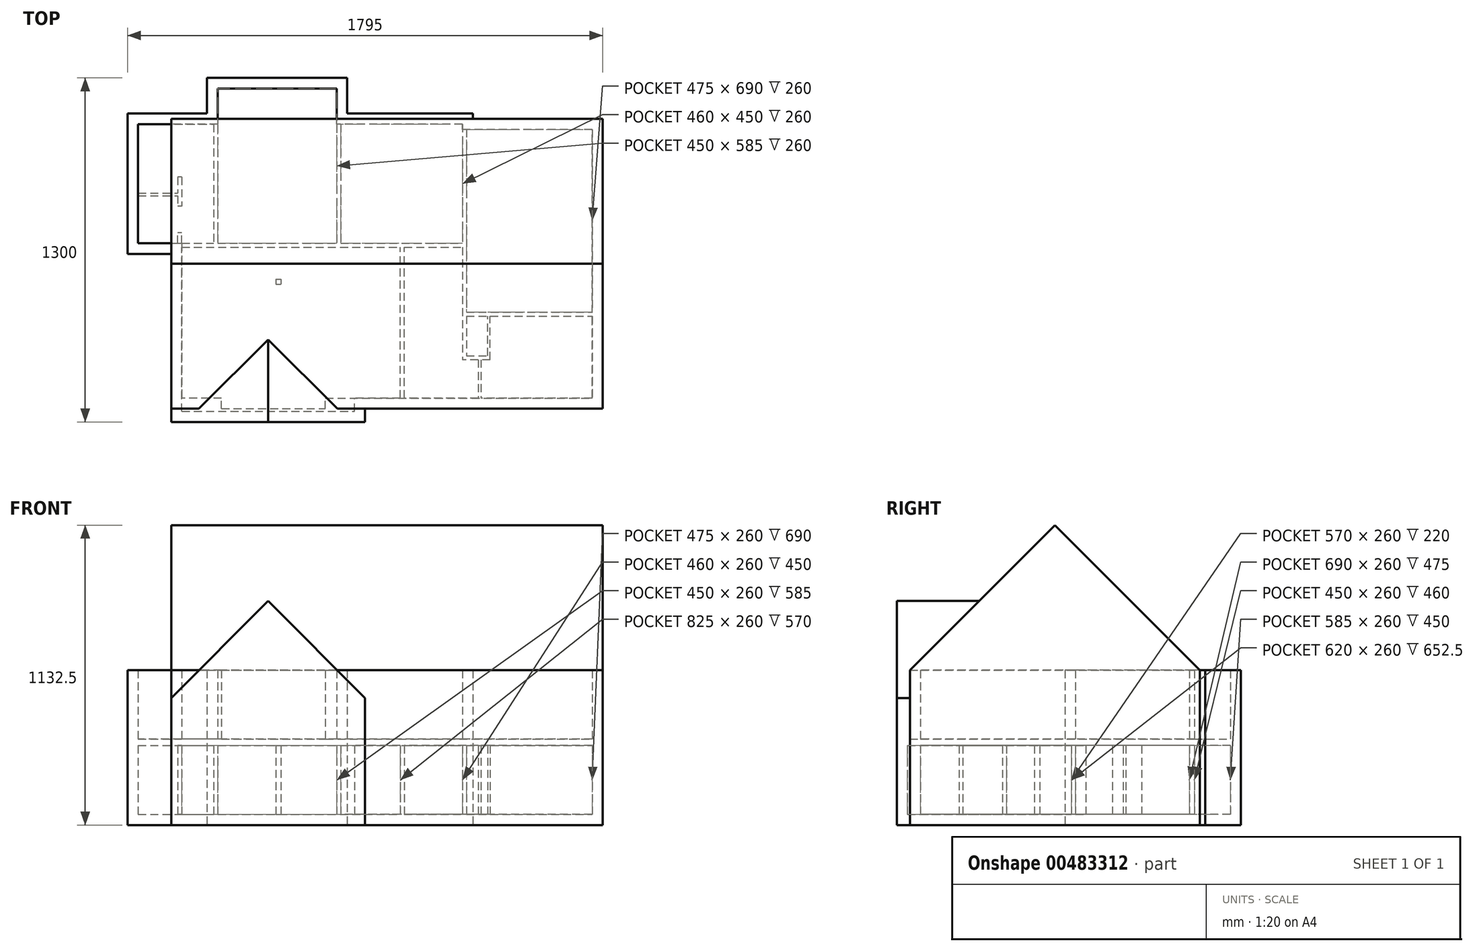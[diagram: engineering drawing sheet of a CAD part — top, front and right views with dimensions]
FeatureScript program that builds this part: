
annotation { "Feature Type Name" : "Feature", "Feature Type Description" : "" }
export const myFeature = defineFeature(function(context is Context, id is Id, definition is map)
    precondition{}
    {
        {
            var Q0;
            Q0=qCreatedBy(makeId("Top.planeOp"),FACE);
            var sketch = newSketch(context, id + "F0", { "sketchPlane" : qUnion([Q0])});
            skLineSegment(sketch, "E0.bottom", {"start": v(-897.5, 650) * mm, "end": v(897.5, 650) * mm});
            skLineSegment(sketch, "E0.top", {"start": v(-897.5, -650) * mm, "end": v(897.5, -650) * mm});
            skLineSegment(sketch, "E0.left", {"start": v(-897.5, 650) * mm, "end": v(-897.5, -650) * mm});
            skLineSegment(sketch, "E0.right", {"start": v(897.5, 650) * mm, "end": v(897.5, -650) * mm});
            skPoint(sketch, "E0.middle", {"position": v(0, 0) * mm});
            skSolve(sketch);
        }
        {
            var Q0;
            Q0 = qSketchRegion(id + "F0", true);
            extrude(context, id + "F1", {"entities" : qUnion([Q0]), "depth" : 300 * mm});
        }
        {
            var Q0;
            Q0=makeQuery(id+"F1.opExtrude","CAP_FACE",FACE,{"disambiguationData":[OSD([sQuery(id+"F0.wireOp",EDGE,"E0.bottom"),sQuery(id+"F0.wireOp",EDGE,"E0.top"),sQuery(id+"F0.wireOp",EDGE,"E0.left"),sQuery(id+"F0.wireOp",EDGE,"E0.right")])],"isStart":true});
            var sketch = newSketch(context, id + "F2", { "sketchPlane" : qUnion([Q0])});
            skLineSegment(sketch, "E1.bottom", {"start": v(-897.5, 650) * mm, "end": v(-732.5, 650) * mm});
            skLineSegment(sketch, "E1.top", {"start": v(-897.5, 15) * mm, "end": v(-732.5, 15) * mm});
            skLineSegment(sketch, "E1.left", {"start": v(-897.5, 650) * mm, "end": v(-897.5, 15) * mm});
            skLineSegment(sketch, "E1.right", {"start": v(-732.5, 650) * mm, "end": v(-732.5, 15) * mm});
            skPoint(sketch, "E2.oppositeSnap0", {"position": v(-732.5, 332.5) * mm});
            skLineSegment(sketch, "E2.bottom", {"start": v(-897.5, -650) * mm, "end": v(-597.5, -650) * mm});
            skLineSegment(sketch, "E2.top", {"start": v(-897.5, -515) * mm, "end": v(-597.5, -515) * mm});
            skLineSegment(sketch, "E2.left", {"start": v(-897.5, -650) * mm, "end": v(-897.5, -515) * mm});
            skLineSegment(sketch, "E2.right", {"start": v(-597.5, -650) * mm, "end": v(-597.5, -515) * mm});
            skLineSegment(sketch, "E3.bottom", {"start": v(897.5, 650) * mm, "end": v(0, 650) * mm});
            skLineSegment(sketch, "E3.top", {"start": v(897.5, 600) * mm, "end": v(0, 600) * mm});
            skLineSegment(sketch, "E3.left", {"start": v(897.5, 650) * mm, "end": v(897.5, 600) * mm});
            skLineSegment(sketch, "E3.right", {"start": v(0, 650) * mm, "end": v(0, 600) * mm});
            skLineSegment(sketch, "E4.bottom", {"start": v(897.5, -650) * mm, "end": v(-67.5, -650) * mm});
            skLineSegment(sketch, "E4.top", {"start": v(897.5, -515) * mm, "end": v(-67.5, -515) * mm});
            skLineSegment(sketch, "E4.left", {"start": v(897.5, -650) * mm, "end": v(897.5, -515) * mm});
            skLineSegment(sketch, "E4.right", {"start": v(-67.5, -650) * mm, "end": v(-67.5, -515) * mm});
            skLineSegment(sketch, "E5.bottom", {"start": v(897.5, -515) * mm, "end": v(407.5, -515) * mm});
            skLineSegment(sketch, "E5.top", {"start": v(897.5, -495) * mm, "end": v(407.5, -495) * mm});
            skLineSegment(sketch, "E5.left", {"start": v(897.5, -515) * mm, "end": v(897.5, -495) * mm});
            skLineSegment(sketch, "E5.right", {"start": v(407.5, -515) * mm, "end": v(407.5, -495) * mm});
            skSolve(sketch);
        }
        {
            var Q0;
            Q0 = qSketchRegion(id + "F2", true);
            extrude(context, id + "F3", {"entities" : qUnion([Q0]), "operationType" : NewBodyOperationType.REMOVE, "oppositeDirection" : true, "depth" : 300 * mm});
        }
        {
            var Q0;
            Q0=makeQuery(id+"F1.opExtrude","CAP_FACE",FACE,{"disambiguationData":[OSD([sQuery(id+"F0.wireOp",EDGE,"E0.bottom"),sQuery(id+"F0.wireOp",EDGE,"E0.top"),sQuery(id+"F0.wireOp",EDGE,"E0.left"),sQuery(id+"F0.wireOp",EDGE,"E0.right")])],"isStart":false});
            shell(context, id + "F4", {"entities" : qUnion([Q0]), "thickness" : 40 * mm});
        }
        {
            var Q0;
            Q0=makeQuery(id+"F4.opShell","OFFSET_FACE",FACE,{"disambiguationData":[OSD([sQuery(id+"F0.wireOp",EDGE,"E0.bottom"),sQuery(id+"F0.wireOp",EDGE,"E0.top"),sQuery(id+"F0.wireOp",EDGE,"E0.left"),sQuery(id+"F0.wireOp",EDGE,"E0.right")])]});
            var sketch = newSketch(context, id + "F5", { "sketchPlane" : qUnion([Q0])});
            skLineSegment(sketch, "E6.bottom", {"start": v(132.5, -560) * mm, "end": v(147.5, -560) * mm});
            skLineSegment(sketch, "E6.left", {"start": v(132.5, -560) * mm, "end": v(132.5, 10) * mm});
            skLineSegment(sketch, "E6.right", {"start": v(147.5, -560) * mm, "end": v(147.5, 10) * mm});
            skLineSegment(sketch, "E7.bottom", {"start": v(382.5, -235) * mm, "end": v(857.5, -235) * mm});
            skLineSegment(sketch, "E7.top", {"start": v(382.5, -250) * mm, "end": v(462.5, -250) * mm});
            skLineSegment(sketch, "E7.right", {"start": v(857.5, -235) * mm, "end": v(857.5, -250) * mm});
            skLineSegment(sketch, "E8.bottom", {"start": v(-692.5, 25) * mm, "end": v(-572.5, 25) * mm});
            skLineSegment(sketch, "E8.top", {"start": v(-692.5, 10) * mm, "end": v(132.5, 10) * mm});
            skLineSegment(sketch, "E8.left", {"start": v(-692.5, 25) * mm, "end": v(-692.5, 10) * mm});
            skLineSegment(sketch, "E9.bottom", {"start": v(-857.5, 205) * mm, "end": v(-707.5, 205) * mm});
            skLineSegment(sketch, "E9.top", {"start": v(-857.5, 215) * mm, "end": v(-707.5, 215) * mm});
            skLineSegment(sketch, "E9.left", {"start": v(-857.5, 215) * mm, "end": v(-857.5, 205) * mm});
            skLineSegment(sketch, "E9.right", {"start": v(-692.5, 215) * mm, "end": v(-692.5, 205) * mm});
            skLineSegment(sketch, "E10.bottom", {"start": v(-107.5, 475) * mm, "end": v(-92.5, 475) * mm});
            skLineSegment(sketch, "E10.left", {"start": v(-107.5, 475) * mm, "end": v(-107.5, 25) * mm});
            skLineSegment(sketch, "E10.right", {"start": v(-92.5, 475) * mm, "end": v(-92.5, 25) * mm});
            skLineSegment(sketch, "E11.bottom", {"start": v(367.5, 455) * mm, "end": v(382.5, 455) * mm});
            skLineSegment(sketch, "E11.left", {"start": v(367.5, 455) * mm, "end": v(367.5, 25) * mm});
            skLineSegment(sketch, "E11.right", {"start": v(382.5, 455) * mm, "end": v(382.5, -235) * mm});
            skLineSegment(sketch, "E12.trimOffspring", {"start": v(382.5, -250) * mm, "end": v(382.5, -400) * mm});
            skLineSegment(sketch, "E13.trimOffspring", {"start": v(-92.5, 25) * mm, "end": v(367.5, 25) * mm});
            skLineSegment(sketch, "E14.bottom", {"start": v(-557.5, 475) * mm, "end": v(-572.5, 475) * mm});
            skLineSegment(sketch, "E14.left", {"start": v(-557.5, 475) * mm, "end": v(-557.5, 25) * mm});
            skLineSegment(sketch, "E14.right", {"start": v(-572.5, 475) * mm, "end": v(-572.5, 25) * mm});
            skLineSegment(sketch, "E15.trimOffspring", {"start": v(-557.5, 25) * mm, "end": v(-107.5, 25) * mm});
            skLineSegment(sketch, "E16.bottom", {"start": v(-692.5, 25) * mm, "end": v(-707.5, 25) * mm});
            skLineSegment(sketch, "E16.top", {"start": v(-692.5, 65) * mm, "end": v(-707.5, 65) * mm});
            skLineSegment(sketch, "E16.left", {"start": v(-692.5, 25) * mm, "end": v(-692.5, 65) * mm});
            skLineSegment(sketch, "E16.right", {"start": v(-707.5, 25) * mm, "end": v(-707.5, 65) * mm});
            skLineSegment(sketch, "E17.bottom", {"start": v(-692.5, 275) * mm, "end": v(-707.5, 275) * mm});
            skLineSegment(sketch, "E17.top", {"start": v(-692.5, 165) * mm, "end": v(-707.5, 165) * mm});
            skLineSegment(sketch, "E17.left", {"start": v(-692.5, 275) * mm, "end": v(-692.5, 165) * mm});
            skLineSegment(sketch, "E17.right", {"start": v(-707.5, 275) * mm, "end": v(-707.5, 215) * mm});
            skLineSegment(sketch, "E18.trimOffspring", {"start": v(-707.5, 205) * mm, "end": v(-707.5, 165) * mm});
            skLineSegment(sketch, "E19.top", {"start": v(147.5, 10) * mm, "end": v(367.5, 10) * mm});
            skLineSegment(sketch, "E20.trimOffspring", {"start": v(367.5, 10) * mm, "end": v(367.5, -415) * mm});
            skLineSegment(sketch, "E21", {"start": v(472.5, -415) * mm, "end": v(472.5, -250) * mm});
            skLineSegment(sketch, "E22", {"start": v(382.5, -400) * mm, "end": v(462.5, -400) * mm});
            skLineSegment(sketch, "E23", {"start": v(462.5, -400) * mm, "end": v(462.5, -250) * mm});
            skLineSegment(sketch, "E24", {"start": v(427.5, -415) * mm, "end": v(427.5, -560) * mm});
            skLineSegment(sketch, "E25", {"start": v(437.5, -415) * mm, "end": v(437.5, -560) * mm});
            skLineSegment(sketch, "E26", {"start": v(472.5, -415) * mm, "end": v(437.5, -415) * mm});
            skLineSegment(sketch, "E27.trimOffspring", {"start": v(427.5, -415) * mm, "end": v(367.5, -415) * mm});
            skLineSegment(sketch, "E28.trimOffspring", {"start": v(472.5, -250) * mm, "end": v(857.5, -250) * mm});
            skLineSegment(sketch, "E29", {"start": v(427.5, -560) * mm, "end": v(437.5, -560) * mm});
            skLineSegment(sketch, "E30.bottom", {"start": v(-337.5, -110) * mm, "end": v(-317.5, -110) * mm});
            skLineSegment(sketch, "E30.top", {"start": v(-337.5, -130) * mm, "end": v(-317.5, -130) * mm});
            skLineSegment(sketch, "E30.left", {"start": v(-337.5, -110) * mm, "end": v(-337.5, -130) * mm});
            skLineSegment(sketch, "E30.right", {"start": v(-317.5, -110) * mm, "end": v(-317.5, -130) * mm});
            skSolve(sketch);
        }
        {
            var Q0;
            Q0 = qSketchRegion(id + "F5", true);
            extrude(context, id + "F6", {"entities" : qUnion([Q0]), "operationType" : NewBodyOperationType.ADD, "depth" : 260 * mm});
        }
        {
            var Q0;
            Q0=makeQuery(id+"F6.boolean.opBoolean","MERGE",FACE,{"derivedFrom":[makeQuery(id+"F1.opExtrude","CAP_FACE",FACE,{"disambiguationData":[OSD([sQuery(id+"F0.wireOp",EDGE,"E0.bottom"),sQuery(id+"F0.wireOp",EDGE,"E0.top"),sQuery(id+"F0.wireOp",EDGE,"E0.left"),sQuery(id+"F0.wireOp",EDGE,"E0.right")])],"isStart":false}),makeQuery(id+"F6.opExtrude","CAP_FACE",FACE,{"disambiguationData":[OSD([sQuery(id+"F5.wireOp",EDGE,"E6.bottom"),sQuery(id+"F5.wireOp",EDGE,"E6.left"),sQuery(id+"F5.wireOp",EDGE,"E6.right"),sQuery(id+"F5.wireOp",EDGE,"E7.bottom"),sQuery(id+"F5.wireOp",EDGE,"E7.top"),sQuery(id+"F5.wireOp",EDGE,"E7.right"),sQuery(id+"F5.wireOp",EDGE,"E8.bottom"),sQuery(id+"F5.wireOp",EDGE,"E8.top"),sQuery(id+"F5.wireOp",EDGE,"E8.left"),sQuery(id+"F5.wireOp",EDGE,"E10.bottom"),sQuery(id+"F5.wireOp",EDGE,"E10.left"),sQuery(id+"F5.wireOp",EDGE,"E10.right"),sQuery(id+"F5.wireOp",EDGE,"E11.bottom"),sQuery(id+"F5.wireOp",EDGE,"E11.left"),sQuery(id+"F5.wireOp",EDGE,"E11.right"),sQuery(id+"F5.wireOp",EDGE,"Mbifjuid-vwa9-f3l3-ZE1X-VHg3meccrZwo"),sQuery(id+"F5.wireOp",EDGE,"E12.trimOffspring"),sQuery(id+"F5.wireOp",EDGE,"E13.trimOffspring"),sQuery(id+"F5.wireOp",EDGE,"E14.bottom"),sQuery(id+"F5.wireOp",EDGE,"E14.left"),sQuery(id+"F5.wireOp",EDGE,"E14.right"),sQuery(id+"F5.wireOp",EDGE,"E15.trimOffspring"),sQuery(id+"F5.wireOp",EDGE,"E19.top"),sQuery(id+"F5.wireOp",EDGE,"E20.trimOffspring")])],"isStart":false}),makeQuery(id+"F6.opExtrude","CAP_FACE",FACE,{"disambiguationData":[OSD([sQuery(id+"F5.wireOp",EDGE,"E9.bottom"),sQuery(id+"F5.wireOp",EDGE,"E9.top"),sQuery(id+"F5.wireOp",EDGE,"E9.left"),sQuery(id+"F5.wireOp",EDGE,"E17.bottom"),sQuery(id+"F5.wireOp",EDGE,"E17.top"),sQuery(id+"F5.wireOp",EDGE,"E17.left"),sQuery(id+"F5.wireOp",EDGE,"E17.right"),sQuery(id+"F5.wireOp",EDGE,"E18.trimOffspring")])],"isStart":false}),makeQuery(id+"F6.opExtrude","CAP_FACE",FACE,{"disambiguationData":[OSD([sQuery(id+"F5.wireOp",EDGE,"E16.bottom"),sQuery(id+"F5.wireOp",EDGE,"E16.top"),sQuery(id+"F5.wireOp",EDGE,"E16.left"),sQuery(id+"F5.wireOp",EDGE,"E16.right")])],"isStart":false})]});
            var sketch = newSketch(context, id + "F7", { "sketchPlane" : qUnion([Q0])});
            skLineSegment(sketch, "E31.0.0", {"start": v(-732.5, -15) * mm, "end": v(-732.5, -650) * mm});
            skLineSegment(sketch, "E31.0.1", {"start": v(-732.5, -650) * mm, "end": v(0, -650) * mm});
            skLineSegment(sketch, "E31.0.2", {"start": v(0, -650) * mm, "end": v(0, -600) * mm});
            skLineSegment(sketch, "E31.0.3", {"start": v(0, -600) * mm, "end": v(897.5, -600) * mm});
            skLineSegment(sketch, "E31.0.4", {"start": v(897.5, -600) * mm, "end": v(897.5, 495) * mm});
            skLineSegment(sketch, "E31.0.5", {"start": v(897.5, 495) * mm, "end": v(407.5, 495) * mm});
            skLineSegment(sketch, "E31.0.6", {"start": v(407.5, 495) * mm, "end": v(407.5, 515) * mm});
            skLineSegment(sketch, "E31.0.7", {"start": v(407.5, 515) * mm, "end": v(-67.5, 515) * mm});
            skLineSegment(sketch, "E31.0.8", {"start": v(-67.5, 515) * mm, "end": v(-67.5, 650) * mm});
            skLineSegment(sketch, "E31.0.9", {"start": v(-67.5, 650) * mm, "end": v(-597.5, 650) * mm});
            skLineSegment(sketch, "E31.0.10", {"start": v(-597.5, 650) * mm, "end": v(-597.5, 515) * mm});
            skLineSegment(sketch, "E31.0.11", {"start": v(-597.5, 515) * mm, "end": v(-897.5, 515) * mm});
            skLineSegment(sketch, "E31.0.12", {"start": v(-897.5, 515) * mm, "end": v(-897.5, -15) * mm});
            skLineSegment(sketch, "E31.0.13", {"start": v(-897.5, -15) * mm, "end": v(-732.5, -15) * mm});
            skSolve(sketch);
        }
        {
            var Q0;
            Q0 = qSketchRegion(id + "F7", true);
            extrude(context, id + "F8", {"entities" : qUnion([Q0]), "operationType" : NewBodyOperationType.ADD, "depth" : 25 * mm});
        }
        {
            var Q0;
            Q0=makeQuery(id+"F8.boolean.opBoolean","MERGE",FACE,{"derivedFrom":[makeQuery(id+"F1.opExtrude","SWEPT_FACE",FACE,{"disambiguationData":[OSD([sQuery(id+"F0.wireOp",EDGE,"E0.top")])]}),makeQuery(id+"F8.opExtrude","SWEPT_FACE",FACE,{"disambiguationData":[OSD([sQuery(id+"F7.wireOp",EDGE,"948ebf68-d73d-4844-9910-1fd970d81693.0.2")])]})]});
            var sketch = newSketch(context, id + "F9", { "sketchPlane" : qUnion([Q0])});
            skLineSegment(sketch, "E32", {"start": v(-732.5, 325) * mm, "end": v(-732.5, 480) * mm});
            skLineSegment(sketch, "E33", {"start": v(-732.5, 480) * mm, "end": v(-366.25, 846.25) * mm});
            skLineSegment(sketch, "E34", {"start": v(-366.25, 846.25) * mm, "end": v(0, 480) * mm});
            skLineSegment(sketch, "E35", {"start": v(0, 480) * mm, "end": v(0, 325) * mm});
            skLineSegment(sketch, "E36.0", {"start": v(-732.5, 325) * mm, "end": v(0, 325) * mm});
            skSolve(sketch);
        }
        {
            var Q0;
            Q0=makeQuery(id+"F9.imprint","IMPRINT",FACE,{"disambiguationData":[TD([[makeQuery(id+"F9.imprint","IMPRINT",EDGE,{"derivedFrom":sQuery(id+"F9.wireOp",EDGE,"E32")}),-1.0]])]});
            extrude(context, id + "F10", {"entities" : qUnion([Q0]), "operationType" : NewBodyOperationType.ADD, "oppositeDirection" : true, "depth" : 50 * mm});
        }
        {
            var Q0;
            Q0=makeQuery(id+"F8.opExtrude","CAP_FACE",FACE,{"disambiguationData":[OSD([sQuery(id+"F7.wireOp",EDGE,"E31.0.0"),sQuery(id+"F7.wireOp",EDGE,"E31.0.1"),sQuery(id+"F7.wireOp",EDGE,"E31.0.2"),sQuery(id+"F7.wireOp",EDGE,"E31.0.3"),sQuery(id+"F7.wireOp",EDGE,"E31.0.4"),sQuery(id+"F7.wireOp",EDGE,"E31.0.5"),sQuery(id+"F7.wireOp",EDGE,"E31.0.6"),sQuery(id+"F7.wireOp",EDGE,"E31.0.7"),sQuery(id+"F7.wireOp",EDGE,"E31.0.8"),sQuery(id+"F7.wireOp",EDGE,"E31.0.9"),sQuery(id+"F7.wireOp",EDGE,"E31.0.10"),sQuery(id+"F7.wireOp",EDGE,"E31.0.11"),sQuery(id+"F7.wireOp",EDGE,"E31.0.12"),sQuery(id+"F7.wireOp",EDGE,"E31.0.13")])],"isStart":false});
            var sketch = newSketch(context, id + "F11", { "sketchPlane" : qUnion([Q0])});
            skLineSegment(sketch, "E37.0.0", {"start": v(-732.5, -15) * mm, "end": v(-732.5, -600) * mm});
            skLineSegment(sketch, "E37.0.2", {"start": v(0, -600) * mm, "end": v(0, -600) * mm});
            skLineSegment(sketch, "E37.0.3", {"start": v(0, -600) * mm, "end": v(897.5, -600) * mm});
            skLineSegment(sketch, "E37.0.4", {"start": v(897.5, -600) * mm, "end": v(897.5, 495) * mm});
            skLineSegment(sketch, "E37.0.5", {"start": v(897.5, 495) * mm, "end": v(407.5, 495) * mm});
            skLineSegment(sketch, "E37.0.6", {"start": v(407.5, 495) * mm, "end": v(407.5, 515) * mm});
            skLineSegment(sketch, "E37.0.7", {"start": v(407.5, 515) * mm, "end": v(-67.5, 515) * mm});
            skLineSegment(sketch, "E37.0.8", {"start": v(-67.5, 515) * mm, "end": v(-67.5, 650) * mm});
            skLineSegment(sketch, "E37.0.9", {"start": v(-67.5, 650) * mm, "end": v(-597.5, 650) * mm});
            skLineSegment(sketch, "E37.0.10", {"start": v(-597.5, 650) * mm, "end": v(-597.5, 515) * mm});
            skLineSegment(sketch, "E37.0.11", {"start": v(-597.5, 515) * mm, "end": v(-897.5, 515) * mm});
            skLineSegment(sketch, "E37.0.12", {"start": v(-897.5, 515) * mm, "end": v(-897.5, -15) * mm});
            skLineSegment(sketch, "E37.0.13", {"start": v(-897.5, -15) * mm, "end": v(-732.5, -15) * mm});
            skLineSegment(sketch, "E38.0", {"start": v(-857.5, 475) * mm, "end": v(-857.5, 25) * mm});
            skLineSegment(sketch, "E39.0", {"start": v(-557.5, 475) * mm, "end": v(-857.5, 475) * mm});
            skLineSegment(sketch, "E40.0", {"start": v(-557.5, 610) * mm, "end": v(-557.5, 475) * mm});
            skLineSegment(sketch, "E41.0", {"start": v(-107.5, 610) * mm, "end": v(-557.5, 610) * mm});
            skLineSegment(sketch, "E42.0", {"start": v(-107.5, 475) * mm, "end": v(-107.5, 610) * mm});
            skLineSegment(sketch, "E43.0", {"start": v(367.5, 475) * mm, "end": v(-107.5, 475) * mm});
            skLineSegment(sketch, "E44.0", {"start": v(367.5, 455) * mm, "end": v(367.5, 475) * mm});
            skLineSegment(sketch, "E45.0", {"start": v(857.5, 455) * mm, "end": v(367.5, 455) * mm});
            skLineSegment(sketch, "E46.0", {"start": v(857.5, -560) * mm, "end": v(857.5, 455) * mm});
            skLineSegment(sketch, "E47.0", {"start": v(-150, -560) * mm, "end": v(857.5, -560) * mm});
            skLineSegment(sketch, "E48.0", {"start": v(-150, -600) * mm, "end": v(-150, -560) * mm});
            skLineSegment(sketch, "E49.0", {"start": v(-857.5, 25) * mm, "end": v(-692.5, 25) * mm});
            skLineSegment(sketch, "E50.0", {"start": v(-692.5, 25) * mm, "end": v(-692.5, -560) * mm});
            skLineSegment(sketch, "E51", {"start": v(-732.5, -600) * mm, "end": v(-692.5, -600) * mm});
            skLineSegment(sketch, "E52", {"start": v(0, -600) * mm, "end": v(-150, -600) * mm});
            skLineSegment(sketch, "E53", {"start": v(-692.5, -600) * mm, "end": v(-542.5, -600) * mm});
            skLineSegment(sketch, "E54", {"start": v(-542.5, -600) * mm, "end": v(-542.5, -560) * mm});
            skLineSegment(sketch, "E55", {"start": v(-542.5, -560) * mm, "end": v(-692.5, -560) * mm});
            skSolve(sketch);
        }
        {
            var Q0;
            Q0 = qSketchRegion(id + "F11", true);
            extrude(context, id + "F12", {"entities" : qUnion([Q0]), "operationType" : NewBodyOperationType.ADD, "depth" : 260 * mm});
        }
        {
            var Q0;
            Q0=makeQuery(id+"F10.opExtrude","CAP_FACE",FACE,{"disambiguationData":[OSD([sQuery(id+"F9.wireOp",EDGE,"E32"),sQuery(id+"F9.wireOp",EDGE,"E33"),sQuery(id+"F9.wireOp",EDGE,"E34"),sQuery(id+"F9.wireOp",EDGE,"E35"),sQuery(id+"F9.wireOp",EDGE,"E36.0")])],"isStart":false});
            var sketch = newSketch(context, id + "F13", { "sketchPlane" : qUnion([Q0])});
            skLineSegment(sketch, "E56.0", {"start": v(366.25, 846.25) * mm, "end": v(105, 585) * mm});
            skLineSegment(sketch, "E57.0", {"start": v(627.5, 585) * mm, "end": v(366.25, 846.25) * mm});
            skLineSegment(sketch, "E58", {"start": v(105, 585) * mm, "end": v(627.5, 585) * mm});
            skSolve(sketch);
        }
        {
            var Q0;
            Q0 = qSketchRegion(id + "F13", true);
            extrude(context, id + "F14", {"entities" : qUnion([Q0]), "operationType" : NewBodyOperationType.ADD, "depth" : 400 * mm});
        }
        {
            var Q0;
            Q0=makeQuery(id+"F12.boolean.opBoolean","MERGE",FACE,{"derivedFrom":[makeQuery(id+"F8.boolean.opBoolean","MERGE",FACE,{"derivedFrom":[makeQuery(id+"F1.opExtrude","SWEPT_FACE",FACE,{"disambiguationData":[OSD([sQuery(id+"F0.wireOp",EDGE,"E0.right")])]}),makeQuery(id+"F8.opExtrude","SWEPT_FACE",FACE,{"disambiguationData":[OSD([sQuery(id+"F7.wireOp",EDGE,"E31.0.4")])]})]}),makeQuery(id+"F12.opExtrude","SWEPT_FACE",FACE,{"disambiguationData":[OSD([sQuery(id+"F11.wireOp",EDGE,"E37.0.4")])]})]});
            var sketch = newSketch(context, id + "F15", { "sketchPlane" : qUnion([Q0])});
            skLineSegment(sketch, "E59", {"start": v(-600, 585) * mm, "end": v(-52.5, 1132.5) * mm});
            skLineSegment(sketch, "E60", {"start": v(-52.5, 1132.5) * mm, "end": v(495, 585) * mm});
            skLineSegment(sketch, "E61.0", {"start": v(495, 585) * mm, "end": v(-600, 585) * mm});
            skSolve(sketch);
        }
        {
            var Q0;
            Q0=makeQuery(id+"F15.imprint","IMPRINT",FACE,{"disambiguationData":[TD([[makeQuery(id+"F15.imprint","IMPRINT",EDGE,{"derivedFrom":sQuery(id+"F15.wireOp",EDGE,"E59")}),-1.0]])]});
            extrude(context, id + "F16", {"entities" : qUnion([Q0]), "operationType" : NewBodyOperationType.ADD, "oppositeDirection" : true, "depth" : 1630 * mm});
        }
    });
